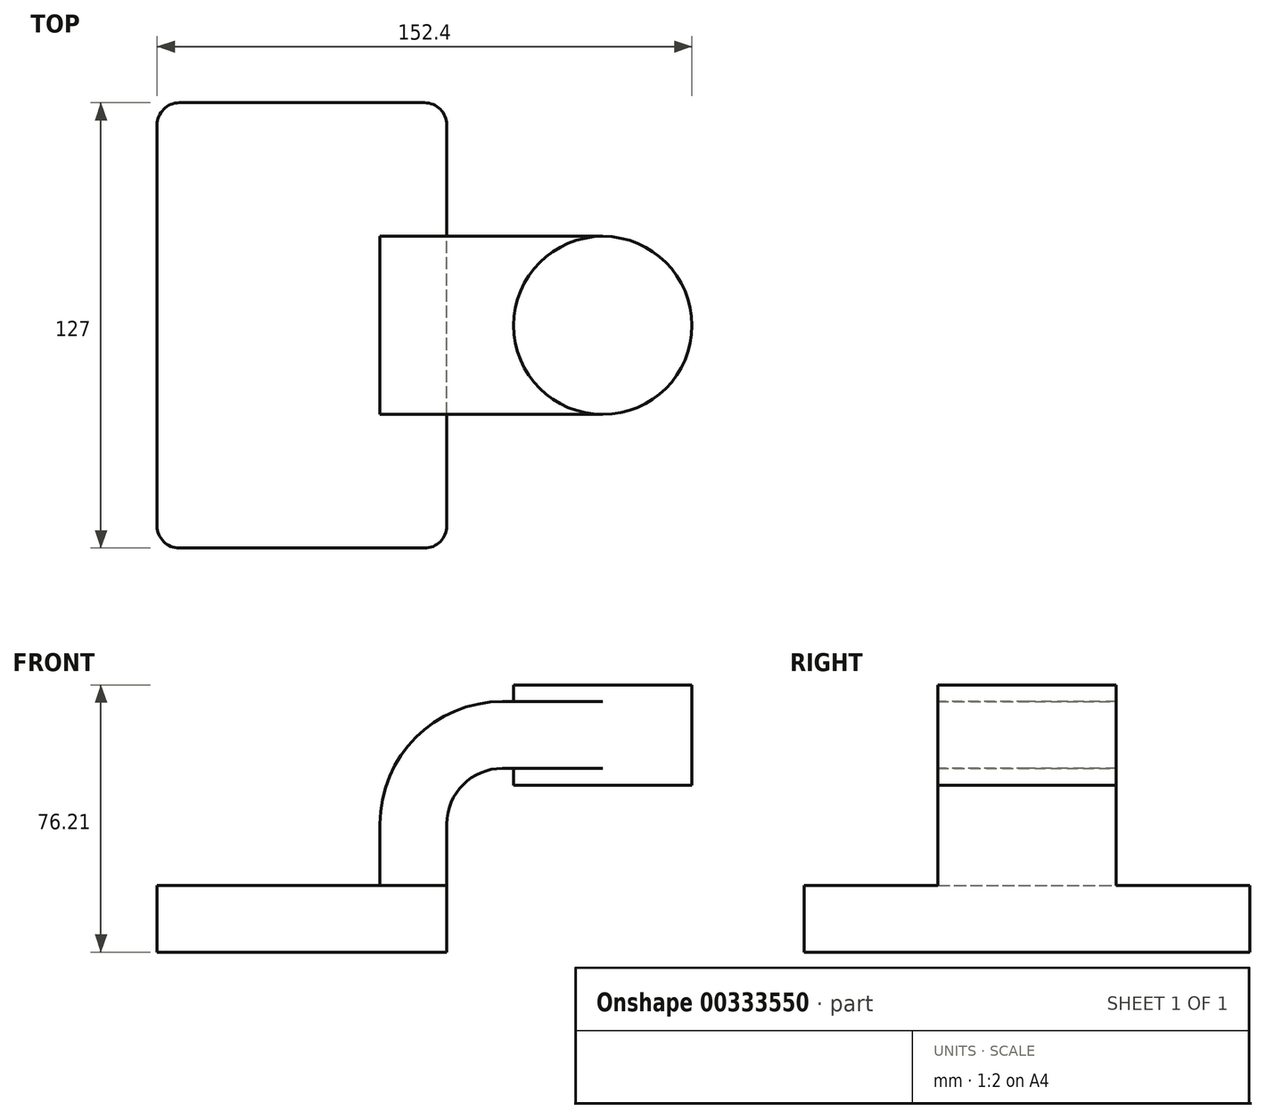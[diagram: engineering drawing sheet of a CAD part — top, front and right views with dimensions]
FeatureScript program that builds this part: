
annotation { "Feature Type Name" : "Feature", "Feature Type Description" : "" }
export const myFeature = defineFeature(function(context is Context, id is Id, definition is map)
    precondition{}
    {
        {
            var Q0;
            Q0=qCreatedBy(makeId("Front.planeOp"),FACE);
            var sketch = newSketch(context, id + "F0", { "sketchPlane" : qUnion([Q0])});
            skLineSegment(sketch, "E0.bottom", {"start": v(-41.28, -9.52) * mm, "end": v(41.28, -9.52) * mm});
            skLineSegment(sketch, "E0.top", {"start": v(-41.28, 9.52) * mm, "end": v(41.28, 9.52) * mm});
            skLineSegment(sketch, "E0.left", {"start": v(-41.28, -9.52) * mm, "end": v(-41.28, 9.52) * mm});
            skLineSegment(sketch, "E0.right", {"start": v(41.28, -9.53) * mm, "end": v(41.28, 9.52) * mm});
            skPoint(sketch, "E0.middle", {"position": v(0, 0) * mm});
            skLineSegment(sketch, "E1.bottom", {"start": v(60.32, 38.1) * mm, "end": v(111.12, 38.1) * mm});
            skLineSegment(sketch, "E1.top", {"start": v(60.32, 66.68) * mm, "end": v(111.12, 66.68) * mm});
            skLineSegment(sketch, "E1.left", {"start": v(60.32, 38.1) * mm, "end": v(60.32, 66.68) * mm});
            skLineSegment(sketch, "E1.right", {"start": v(111.12, 38.1) * mm, "end": v(111.12, 66.68) * mm});
            skPoint(sketch, "E1.middle", {"position": v(85.72, 52.39) * mm});
            skLineSegment(sketch, "E2", {"start": v(41.27, 9.52) * mm, "end": v(41.27, 27) * mm});
            skArc(sketch, "E3", {"start": v(41.27, 27) * mm, "mid": v(45.92, 38.23) * mm, "end": v(57.15, 42.88) * mm});
            skLineSegment(sketch, "E4", {"start": v(57.15, 42.88) * mm, "end": v(85.72, 42.88) * mm});
            skLineSegment(sketch, "E5.0", {"start": v(57.15, 61.93) * mm, "end": v(85.72, 61.93) * mm});
            skArc(sketch, "E5.1", {"start": v(22.23, 27) * mm, "mid": v(32.45, 51.7) * mm, "end": v(57.15, 61.93) * mm});
            skLineSegment(sketch, "E5.2", {"start": v(22.22, 9.52) * mm, "end": v(22.22, 27) * mm});
            skLineSegment(sketch, "E6", {"start": v(85.72, 38.1) * mm, "end": v(85.72, 66.68) * mm});
            skFitSpline(sketch, "E7", {"points": [v(-41.28, 9.53) * mm, v(57.15, 61.93) * mm], "startDerivative": vector(-4.47, 68.8) * mm, "endDerivative": vector(128.75, -6.7) * mm});
            skSolve(sketch);
        }
        {
            var Q0;
            Q0=makeQuery(id+"F0.imprint","IMPRINT",FACE,{"disambiguationData":[TD([[makeQuery(id+"F0.imprint","IMPRINT",EDGE,{"derivedFrom":sQuery(id+"F0.wireOp",EDGE,"E0.bottom")}),1.0]])]});
            extrude(context, id + "F1", {"entities" : qUnion([Q0]), "endBound" : BoundingType.SYMMETRIC, "depth" : 127 * mm});
        }
        {
            var Q0;
            {var subQ1=sQuery(id+"F0.wireOp",EDGE,"E2");Q0=makeQuery(id+"F0.imprint","IMPRINT",FACE,{"disambiguationData":[TD([[makeQuery(id+"F0.imprint","IMPRINT",EDGE,{"derivedFrom":subQ1}),1.0]])]});}
            var Q1;
            {var subQ0=sQuery(id+"F0.wireOp",EDGE,"E4");var subQ1=sQuery(id+"F0.wireOp",EDGE,"E1.left");var subQ2=makeQuery(id+"F0.imprint","INTERSECT",VERTEX,{"derivedFrom":[subQ1,subQ0]});Q1=makeQuery(id+"F0.imprint","IMPRINT",FACE,{"disambiguationData":[TD([[makeQuery(id+"F0.imprint","IMPRINT",EDGE,{"disambiguationData":[TD([[subQ2,-1.0]])],"derivedFrom":subQ1}),-1.0]])]});}
            extrude(context, id + "F2", {"entities" : qUnion([Q0, Q1]), "operationType" : NewBodyOperationType.ADD, "endBound" : BoundingType.SYMMETRIC, "depth" : 50.8 * mm});
        }
        {
            var Q0;
            Q0=makeQuery(id+"F0.imprint","IMPRINT",FACE,{"disambiguationData":[TD([[makeQuery(id+"F0.imprint","IMPRINT",EDGE,{"derivedFrom":sQuery(id+"F0.wireOp",EDGE,"E5.1")}),1.0]])]});
            extrude(context, id + "F3", {"entities" : qUnion([Q0]), "operationType" : NewBodyOperationType.ADD, "endBound" : BoundingType.SYMMETRIC, "depth" : 15.88 * mm});
        }
        {
            var Q0;
            {var subQ0=sQuery(id+"F0.wireOp",EDGE,"E1.right");Q0=makeQuery(id+"F0.imprint","IMPRINT",FACE,{"disambiguationData":[TD([[makeQuery(id+"F0.imprint","IMPRINT",EDGE,{"derivedFrom":subQ0}),1.0]])]});}
            var Q1;
            Q1=sQuery(id+"F0.wireOp",EDGE,"E6");
            revolve(context, id + "F4", {"operationType" : NewBodyOperationType.ADD, "entities" : qUnion([Q0]), "axis" : qUnion([Q1]), "revolveType" : RevolveType.FULL});
        }
        {
            var Q0;
            Q0=makeQuery(id+"F1.opExtrude","CAP_EDGE",EDGE,{"disambiguationData":[OSD([sQuery(id+"F0.wireOp",EDGE,"E0.right")])],"isStart":true});
            var Q1;
            Q1=makeQuery(id+"F1.opExtrude","CAP_EDGE",EDGE,{"disambiguationData":[OSD([sQuery(id+"F0.wireOp",EDGE,"E0.right")])],"isStart":false});
            var Q2;
            Q2=makeQuery(id+"F1.opExtrude","CAP_EDGE",EDGE,{"disambiguationData":[OSD([sQuery(id+"F0.wireOp",EDGE,"E0.left")])],"isStart":false});
            var Q3;
            Q3=makeQuery(id+"F1.opExtrude","CAP_EDGE",EDGE,{"disambiguationData":[OSD([sQuery(id+"F0.wireOp",EDGE,"E0.left")])],"isStart":true});
            fillet(context, id + "F5", {"entities" : qUnion([Q0, Q1, Q2, Q3]), "radius" : 6.35 * mm, "tangentPropagation" : true, "allowEdgeOverflow" : false});
        }
    });
